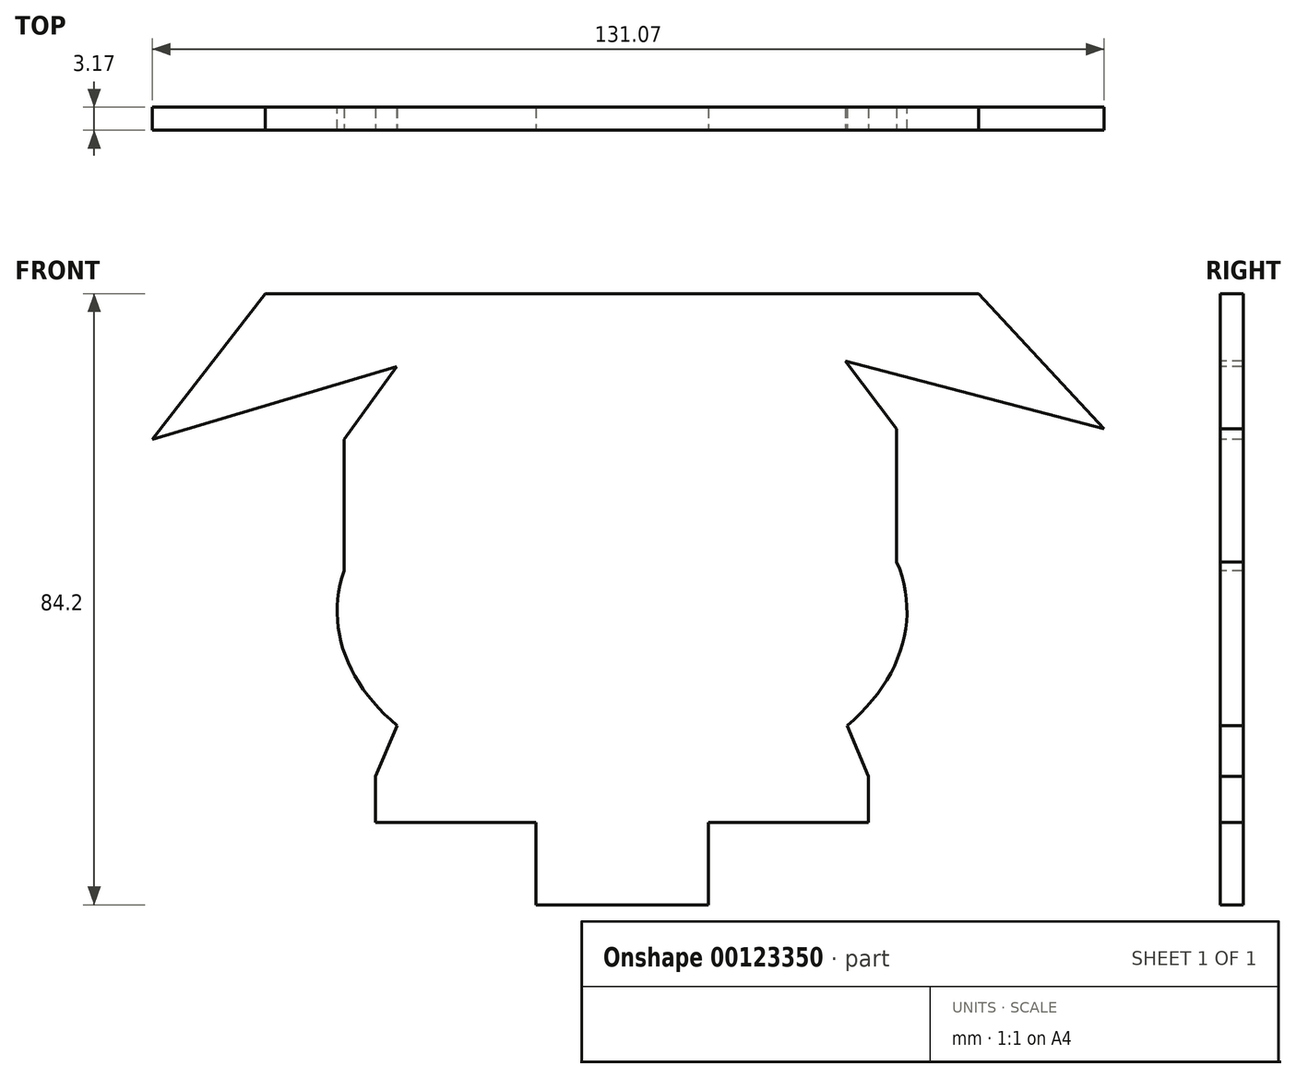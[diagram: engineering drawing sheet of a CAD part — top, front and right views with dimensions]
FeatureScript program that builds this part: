
annotation { "Feature Type Name" : "Feature", "Feature Type Description" : "" }
export const myFeature = defineFeature(function(context is Context, id is Id, definition is map)
    precondition{}
    {
        {
            var Q0;
            Q0=qCreatedBy(makeId("Front.planeOp"),FACE);
            var sketch = newSketch(context, id + "F0", { "sketchPlane" : qUnion([Q0])});
            skEllipse(sketch, "E0", {"center": v(0, 57.15) * mm, "majorRadius": 23.72 * mm, "minorRadius": 13.39 * mm, "majorAxis": v(1, 0)});
            skEllipticalArc(sketch, "E1", {});
            skLineSegment(sketch, "E2", {"start": v(0, 43.76) * mm, "end": v(0, 38.81) * mm});
            skArc(sketch, "E3", {"start": v(-23.72, 38.81) * mm, "mid": v(-11.86, 31.98) * mm, "end": v(0, 38.81) * mm});
            skPoint(sketch, "E3.startSnap0", {"position": v(-23.72, 57.15) * mm});
            skArc(sketch, "E4", {"start": v(0, 38.81) * mm, "mid": v(11.86, 32.02) * mm, "end": v(23.72, 38.81) * mm});
            skPoint(sketch, "E4.endSnap0", {"position": v(23.72, 57.15) * mm});
            skLineSegment(sketch, "E5.top", {"start": v(-23.72, 95.34) * mm, "end": v(23.72, 95.34) * mm});
            skLineSegment(sketch, "E5.left", {"start": v(-38.3, 57.15) * mm, "end": v(-38.3, 75.28) * mm});
            skLineSegment(sketch, "E5.right", {"start": v(37.83, 58.04) * mm, "end": v(37.83, 76.7) * mm});
            skArc(sketch, "E6", {"start": v(23.72, 72.03) * mm, "mid": v(14.8, 88.03) * mm, "end": v(0, 77.25) * mm});
            skArc(sketch, "E7", {"start": v(0, 77.25) * mm, "mid": v(-14.97, 88.75) * mm, "end": v(-23.72, 72.03) * mm});
            skLineSegment(sketch, "E8", {"start": v(-38.3, 75.28) * mm, "end": v(-31, 85.31) * mm});
            skLineSegment(sketch, "E9", {"start": v(37.83, 76.7) * mm, "end": v(30.77, 86.03) * mm});
            skLineSegment(sketch, "E10", {"start": v(-30.98, 35.84) * mm, "end": v(-33.97, 28.85) * mm});
            skLineSegment(sketch, "E11", {"start": v(30.98, 35.84) * mm, "end": v(33.93, 28.85) * mm});
            skLineSegment(sketch, "E12.top", {"start": v(-33.97, 11.14) * mm, "end": v(33.93, 11.14) * mm});
            skLineSegment(sketch, "E12.left", {"start": v(-33.97, 28.85) * mm, "end": v(-33.97, 11.14) * mm});
            skLineSegment(sketch, "E12.right", {"start": v(33.93, 28.85) * mm, "end": v(33.93, 11.14) * mm});
            skPoint(sketch, "E13.oppositeSnap0", {"position": v(-11.86, 31.98) * mm});
            skLineSegment(sketch, "E13.bottom", {"start": v(-33.97, 11.14) * mm, "end": v(-11.86, 11.14) * mm});
            skLineSegment(sketch, "E13.top", {"start": v(-33.97, 22.5) * mm, "end": v(-11.86, 22.5) * mm});
            skLineSegment(sketch, "E13.left", {"start": v(-33.97, 11.14) * mm, "end": v(-33.97, 22.5) * mm});
            skLineSegment(sketch, "E13.right", {"start": v(-11.86, 11.14) * mm, "end": v(-11.86, 22.5) * mm});
            skPoint(sketch, "E14.oppositeSnap0", {"position": v(11.86, 32.02) * mm});
            skLineSegment(sketch, "E14.bottom", {"start": v(33.93, 11.14) * mm, "end": v(11.86, 11.14) * mm});
            skLineSegment(sketch, "E14.top", {"start": v(33.93, 22.5) * mm, "end": v(11.86, 22.5) * mm});
            skLineSegment(sketch, "E14.left", {"start": v(33.93, 11.14) * mm, "end": v(33.93, 22.5) * mm});
            skLineSegment(sketch, "E14.right", {"start": v(11.86, 11.14) * mm, "end": v(11.86, 22.5) * mm});
            skLineSegment(sketch, "E15", {"start": v(23.72, 95.34) * mm, "end": v(49.12, 95.34) * mm});
            skLineSegment(sketch, "E16", {"start": v(-23.72, 95.34) * mm, "end": v(-49.12, 95.34) * mm});
            skLineSegment(sketch, "E17", {"start": v(-49.12, 95.34) * mm, "end": v(-64.7, 75.28) * mm});
            skLineSegment(sketch, "E18", {"start": v(-64.7, 75.28) * mm, "end": v(-31, 85.31) * mm});
            skLineSegment(sketch, "E19", {"start": v(49.12, 95.34) * mm, "end": v(66.38, 76.7) * mm});
            skLineSegment(sketch, "E20", {"start": v(66.38, 76.7) * mm, "end": v(30.77, 86.03) * mm});
            const initialGuessF0  = {"E1": [0, 0.05158504677399959, 1, 0, 0.039232422363036604, 0.025664466305332104, 5.6227254887037565, 3.8020524720656232]};
            skSetInitialGuess(sketch, initialGuessF0);
            skSolve(sketch);
        }
        {
            var Q0;
            {var subQ0=sQuery(id+"F0.wireOp",EDGE,"E7");Q0=makeQuery(id+"F0.imprint","IMPRINT",FACE,{"disambiguationData":[TD([[makeQuery(id+"F0.imprint","IMPRINT",EDGE,{"derivedFrom":subQ0}),1.0]])]});}
            var Q1;
            Q1=makeQuery(id+"F0.imprint","IMPRINT",FACE,{"disambiguationData":[TD([[makeQuery(id+"F0.imprint","IMPRINT",EDGE,{"derivedFrom":sQuery(id+"F0.wireOp",EDGE,"E0")}),-1.0]])]});
            var Q2;
            {var subQ1=sQuery(id+"F0.wireOp",EDGE,"E10");Q2=makeQuery(id+"F0.imprint","IMPRINT",FACE,{"disambiguationData":[TD([[makeQuery(id+"F0.imprint","IMPRINT",EDGE,{"derivedFrom":subQ1}),1.0]])]});}
            var Q3;
            Q3=makeQuery(id+"F0.imprint","IMPRINT",FACE,{"disambiguationData":[TD([[makeQuery(id+"F0.imprint","IMPRINT",EDGE,{"derivedFrom":sQuery(id+"F0.wireOp",EDGE,"E14.bottom")}),-1.0]])]});
            var Q4;
            {var subQ0=sQuery(id+"F0.wireOp",EDGE,"E6");Q4=makeQuery(id+"F0.imprint","IMPRINT",FACE,{"disambiguationData":[TD([[makeQuery(id+"F0.imprint","IMPRINT",EDGE,{"derivedFrom":subQ0}),1.0]])]});}
            var Q5;
            Q5=makeQuery(id+"F0.imprint","IMPRINT",FACE,{"disambiguationData":[TD([[makeQuery(id+"F0.imprint","IMPRINT",EDGE,{"derivedFrom":sQuery(id+"F0.wireOp",EDGE,"E0")}),1.0]])]});
            var Q6;
            {var subQ4=sQuery(id+"F0.wireOp",EDGE,"E5.top");Q6=makeQuery(id+"F0.imprint","IMPRINT",FACE,{"disambiguationData":[TD([[makeQuery(id+"F0.imprint","IMPRINT",EDGE,{"derivedFrom":subQ4}),-1.0]])]});}
            var Q7;
            Q7=makeQuery(id+"F0.imprint","IMPRINT",FACE,{"disambiguationData":[TD([[makeQuery(id+"F0.imprint","IMPRINT",EDGE,{"derivedFrom":sQuery(id+"F0.wireOp",EDGE,"E13.bottom")}),1.0]])]});
            var Q8;
            {var subQ0=sQuery(id+"F0.wireOp",EDGE,"E15");Q8=makeQuery(id+"F0.imprint","IMPRINT",FACE,{"disambiguationData":[TD([[makeQuery(id+"F0.imprint","IMPRINT",EDGE,{"derivedFrom":subQ0}),-1.0]])]});}
            var Q9;
            {var subQ0=sQuery(id+"F0.wireOp",EDGE,"E16");Q9=makeQuery(id+"F0.imprint","IMPRINT",FACE,{"disambiguationData":[TD([[makeQuery(id+"F0.imprint","IMPRINT",EDGE,{"derivedFrom":subQ0}),1.0]])]});}
            extrude(context, id + "F1", {"entities" : qUnion([Q0, Q1, Q2, Q3, Q4, Q5, Q6, Q7, Q8, Q9]), "oppositeDirection" : true, "depth" : 3.17 * mm});
        }
    });
